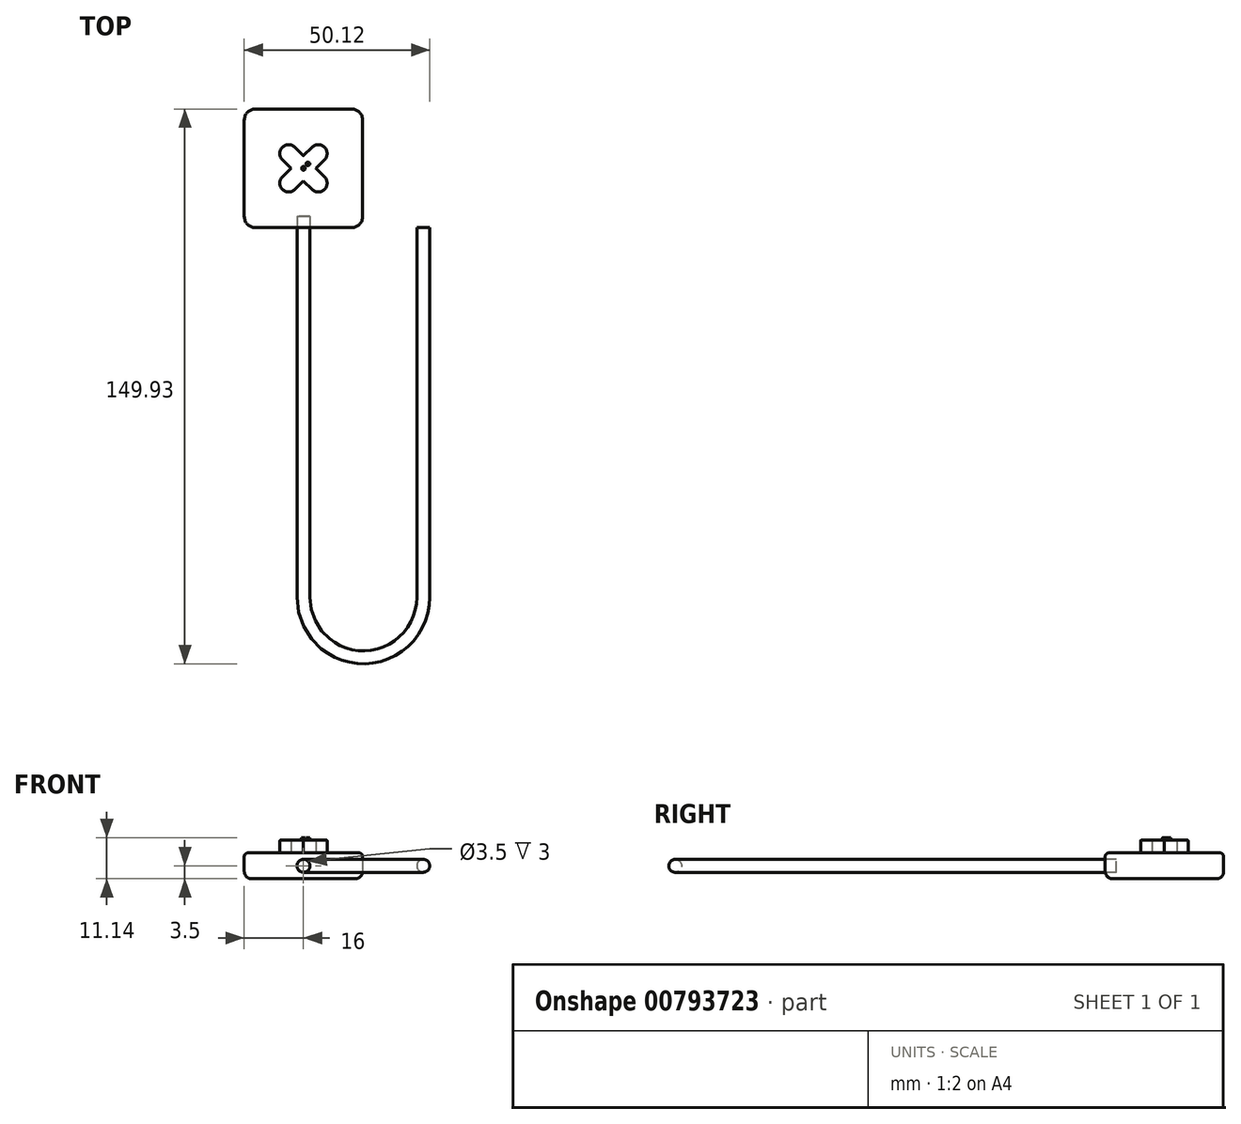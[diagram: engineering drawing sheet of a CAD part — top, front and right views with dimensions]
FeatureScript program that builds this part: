
annotation { "Feature Type Name" : "Feature", "Feature Type Description" : "" }
export const myFeature = defineFeature(function(context is Context, id is Id, definition is map)
    precondition{}
    {
        {
            var Q0;
            Q0=qCreatedBy(makeId("Top.planeOp"),FACE);
            var sketch = newSketch(context, id + "F0", { "sketchPlane" : qUnion([Q0])});
            skLineSegment(sketch, "E0.bottom", {"start": v(-13, 16) * mm, "end": v(13, 16) * mm});
            skLineSegment(sketch, "E0.top", {"start": v(-13, -16) * mm, "end": v(13, -16) * mm});
            skLineSegment(sketch, "E0.left", {"start": v(-16, 13) * mm, "end": v(-16, -13) * mm});
            skLineSegment(sketch, "E0.right", {"start": v(16, 13) * mm, "end": v(16, -13) * mm});
            skPoint(sketch, "E1.visualSharp", {"position": v(16, 16) * mm});
            skArc(sketch, "E1.filletArc", {"start": v(16, 13) * mm, "mid": v(15.12, 15.12) * mm, "end": v(13, 16) * mm});
            skPoint(sketch, "E2.visualSharp", {"position": v(16, -16) * mm});
            skArc(sketch, "E2.filletArc", {"start": v(13, -16) * mm, "mid": v(15.12, -15.12) * mm, "end": v(16, -13) * mm});
            skPoint(sketch, "E3.visualSharp", {"position": v(-16, -16) * mm});
            skArc(sketch, "E3.filletArc", {"start": v(-16, -13) * mm, "mid": v(-15.12, -15.12) * mm, "end": v(-13, -16) * mm});
            skPoint(sketch, "E4.visualSharp", {"position": v(-16, 16) * mm});
            skArc(sketch, "E4.filletArc", {"start": v(-13, 16) * mm, "mid": v(-15.12, 15.12) * mm, "end": v(-16, 13) * mm});
            skPoint(sketch, "E5", {"position": v(0, 16) * mm});
            skPoint(sketch, "E6", {"position": v(16, 0) * mm});
            skSolve(sketch);
        }
        {
            var Q0;
            Q0=makeQuery(id+"F0.imprint","IMPRINT",FACE,{"disambiguationData":[TD([[makeQuery(id+"F0.imprint","IMPRINT",EDGE,{"derivedFrom":sQuery(id+"F0.wireOp",EDGE,"E0.bottom")}),-1.0]])]});
            extrude(context, id + "F1", {"entities" : qUnion([Q0]), "depth" : 7 * mm, "offsetDistance" : 25 * mm});
        }
        {
            var Q0;
            Q0=makeQuery(id+"F1.opExtrude","CAP_FACE",FACE,{"disambiguationData":[OSD([sQuery(id+"F0.wireOp",EDGE,"E0.bottom"),sQuery(id+"F0.wireOp",EDGE,"E0.top"),sQuery(id+"F0.wireOp",EDGE,"E0.left"),sQuery(id+"F0.wireOp",EDGE,"E0.right"),sQuery(id+"F0.wireOp",EDGE,"E1.filletArc"),sQuery(id+"F0.wireOp",EDGE,"E2.filletArc"),sQuery(id+"F0.wireOp",EDGE,"E3.filletArc"),sQuery(id+"F0.wireOp",EDGE,"E4.filletArc")])],"isStart":false});
            var sketch = newSketch(context, id + "F2", { "sketchPlane" : qUnion([Q0])});
            skArc(sketch, "E7", {"start": v(-2.3, 5.7) * mm, "mid": v(-5.7, 5.7) * mm, "end": v(-5.7, 2.3) * mm});
            skArc(sketch, "E8", {"start": v(5.7, 2.3) * mm, "mid": v(5.7, 5.7) * mm, "end": v(2.3, 5.7) * mm});
            skArc(sketch, "E9", {"start": v(2.3, -5.7) * mm, "mid": v(5.7, -5.7) * mm, "end": v(5.7, -2.3) * mm});
            skArc(sketch, "E10", {"start": v(-5.7, -2.3) * mm, "mid": v(-5.7, -5.7) * mm, "end": v(-2.3, -5.7) * mm});
            skPoint(sketch, "E11", {"position": v(0, 0) * mm});
            skLineSegment(sketch, "E12", {"start": v(-5.7, 2.3) * mm, "end": v(-3.4, 0) * mm});
            skLineSegment(sketch, "E13", {"start": v(-2.3, 5.7) * mm, "end": v(0, 3.4) * mm});
            skLineSegment(sketch, "E14", {"start": v(2.3, 5.7) * mm, "end": v(0, 3.4) * mm});
            skLineSegment(sketch, "E15", {"start": v(5.7, 2.3) * mm, "end": v(3.4, 0) * mm});
            skLineSegment(sketch, "E16.trimOffspring", {"start": v(-3.4, 0) * mm, "end": v(-5.7, -2.3) * mm});
            skLineSegment(sketch, "E17.trimOffspring", {"start": v(3.4, 0) * mm, "end": v(5.7, -2.3) * mm});
            skLineSegment(sketch, "E18.trimOffspring", {"start": v(0, -3.4) * mm, "end": v(2.3, -5.7) * mm});
            skLineSegment(sketch, "E19.trimOffspring", {"start": v(0, -3.4) * mm, "end": v(-2.3, -5.7) * mm});
            skSolve(sketch);
        }
        {
            var Q0;
            Q0=makeQuery(id+"F2.imprint","IMPRINT",FACE,{"disambiguationData":[TD([[makeQuery(id+"F2.imprint","IMPRINT",EDGE,{"derivedFrom":sQuery(id+"F2.wireOp",EDGE,"E7")}),1.0]])]});
            extrude(context, id + "F3", {"entities" : qUnion([Q0]), "operationType" : NewBodyOperationType.ADD, "depth" : 3.4 * mm, "offsetDistance" : 25 * mm});
        }
        {
            var Q0;
            Q0=makeQuery(id+"F3.opExtrude","CAP_FACE",FACE,{"disambiguationData":[OSD([sQuery(id+"F2.wireOp",EDGE,"E7"),sQuery(id+"F2.wireOp",EDGE,"E8"),sQuery(id+"F2.wireOp",EDGE,"E9"),sQuery(id+"F2.wireOp",EDGE,"E10"),sQuery(id+"F2.wireOp",EDGE,"E12"),sQuery(id+"F2.wireOp",EDGE,"E13"),sQuery(id+"F2.wireOp",EDGE,"E14"),sQuery(id+"F2.wireOp",EDGE,"E15"),sQuery(id+"F2.wireOp",EDGE,"E16.trimOffspring"),sQuery(id+"F2.wireOp",EDGE,"E17.trimOffspring"),sQuery(id+"F2.wireOp",EDGE,"E18.trimOffspring"),sQuery(id+"F2.wireOp",EDGE,"E19.trimOffspring")])],"isStart":false});
            var sketch = newSketch(context, id + "F4", { "sketchPlane" : qUnion([Q0])});
            skCircle(sketch, "E20", {"center": v(0, 0) * mm, "radius": 0.5 * mm});
            skCircle(sketch, "E21", {"center": v(1.2, 1.2) * mm, "radius": 0.5 * mm});
            skLineSegment(sketch, "E22", {"start": v(0, 0) * mm, "end": v(5.7, 5.7) * mm});
            skSolve(sketch);
        }
        {
            var Q0;
            Q0=makeQuery(id+"F4.imprint","IMPRINT",FACE,{"disambiguationData":[TD([[makeQuery(id+"F4.imprint","IMPRINT",EDGE,{"derivedFrom":sQuery(id+"F4.wireOp",EDGE,"E20")}),1.0]])]});
            var Q1;
            {var subQ0=sQuery(id+"F4.wireOp",EDGE,"E22");var subQ1=sQuery(id+"F4.wireOp",EDGE,"E21");var subQ2=makeQuery(id+"F4.imprint","INTERSECT",VERTEX,{"disambiguationData":[OD(0.0)],"derivedFrom":[subQ1,subQ0]});Q1=makeQuery(id+"F4.imprint","IMPRINT",FACE,{"disambiguationData":[TD([[makeQuery(id+"F4.imprint","IMPRINT",EDGE,{"disambiguationData":[TD([[subQ2,-1.0]])],"derivedFrom":subQ1}),1.0]])]});}
            var Q2;
            {var subQ0=sQuery(id+"F4.wireOp",EDGE,"E22");var subQ1=sQuery(id+"F4.wireOp",EDGE,"E21");var subQ2=makeQuery(id+"F4.imprint","INTERSECT",VERTEX,{"disambiguationData":[OD(0.0)],"derivedFrom":[subQ1,subQ0]});Q2=makeQuery(id+"F4.imprint","IMPRINT",FACE,{"disambiguationData":[TD([[makeQuery(id+"F4.imprint","IMPRINT",EDGE,{"disambiguationData":[TD([[subQ2,1.0]])],"derivedFrom":subQ1}),1.0]])]});}
            extrude(context, id + "F5", {"entities" : qUnion([Q0, Q1, Q2]), "operationType" : NewBodyOperationType.ADD, "depth" : 0.74 * mm, "offsetDistance" : 25 * mm});
        }
        {
            var Q0;
            Q0=makeQuery(id+"F1.opExtrude","SWEPT_FACE",FACE,{"disambiguationData":[OSD([sQuery(id+"F0.wireOp",EDGE,"E0.top")])]});
            var sketch = newSketch(context, id + "F6", { "sketchPlane" : qUnion([Q0])});
            skCircle(sketch, "E23", {"center": v(0, 3.5) * mm, "radius": 1.75 * mm});
            skSolve(sketch);
        }
        {
            var Q0;
            Q0 = qSketchRegion(id + "F6", true);
            extrude(context, id + "F7", {"entities" : qUnion([Q0]), "operationType" : NewBodyOperationType.REMOVE, "oppositeDirection" : true, "depth" : 3 * mm, "offsetDistance" : 25 * mm});
        }
        {
            var Q0;
            Q0=makeQuery(id+"F1.opExtrude","CAP_EDGE",EDGE,{"disambiguationData":[OSD([sQuery(id+"F0.wireOp",EDGE,"E0.top")])],"isStart":true});
            fillet(context, id + "F8", {"entities" : qUnion([Q0]), "radius" : 2 * mm, "tangentPropagation" : true, "allowEdgeOverflow" : false});
        }
        {
            var Q0;
            Q0=makeQuery(id+"F1.opExtrude","CAP_EDGE",EDGE,{"disambiguationData":[OSD([sQuery(id+"F0.wireOp",EDGE,"E0.top")])],"isStart":false});
            fillet(context, id + "F9", {"entities" : qUnion([Q0]), "radius" : 1 * mm, "tangentPropagation" : true, "allowEdgeOverflow" : false});
        }
        {
            var Q0;
            Q0=makeQuery(id+"F3.opExtrude","CAP_EDGE",EDGE,{"disambiguationData":[OSD([sQuery(id+"F2.wireOp",EDGE,"E19.trimOffspring")])],"isStart":false});
            var Q1;
            Q1=makeQuery(id+"F3.opExtrude","CAP_EDGE",EDGE,{"disambiguationData":[OSD([sQuery(id+"F2.wireOp",EDGE,"E18.trimOffspring")])],"isStart":false});
            var Q2;
            Q2=makeQuery(id+"F3.opExtrude","CAP_EDGE",EDGE,{"disambiguationData":[OSD([sQuery(id+"F2.wireOp",EDGE,"E15")])],"isStart":false});
            var Q3;
            Q3=makeQuery(id+"F3.opExtrude","CAP_EDGE",EDGE,{"disambiguationData":[OSD([sQuery(id+"F2.wireOp",EDGE,"E13")])],"isStart":false});
            fillet(context, id + "F10", {"entities" : qUnion([Q0, Q1, Q2, Q3]), "radius" : 0.1 * mm, "tangentPropagation" : true, "allowEdgeOverflow" : false});
        }
        {
            var Q0;
            Q0=qCreatedBy(makeId("Top.planeOp"),FACE);
            var sketch = newSketch(context, id + "F11", { "sketchPlane" : qUnion([Q0])});
            skLineSegment(sketch, "E24", {"start": v(-1.32, -16) * mm, "end": v(-1.32, -116) * mm});
            skLineSegment(sketch, "E25", {"start": v(33.68, -16) * mm, "end": v(33.68, -116) * mm});
            skArc(sketch, "E26", {"start": v(-1.32, -116) * mm, "mid": v(16.18, -133.5) * mm, "end": v(33.68, -116) * mm});
            skSolve(sketch);
        }
        {
            var Q0;
            Q0=makeQuery(id+"F6.imprint","IMPRINT",FACE,{"disambiguationData":[TD([[makeQuery(id+"F6.imprint","IMPRINT",EDGE,{"derivedFrom":sQuery(id+"F6.wireOp",EDGE,"E23")}),1.0]])]});
            var Q1;
            Q1=sQuery(id+"F11.wireOp",EDGE,"E24");
            var Q2;
            Q2=sQuery(id+"F11.wireOp",EDGE,"E26");
            var Q3;
            Q3=sQuery(id+"F11.wireOp",EDGE,"E25");
            sweep(context, id + "F12", {"profiles" : qUnion([Q0]), "path" : qUnion([Q1, Q2, Q3])});
        }
    });
